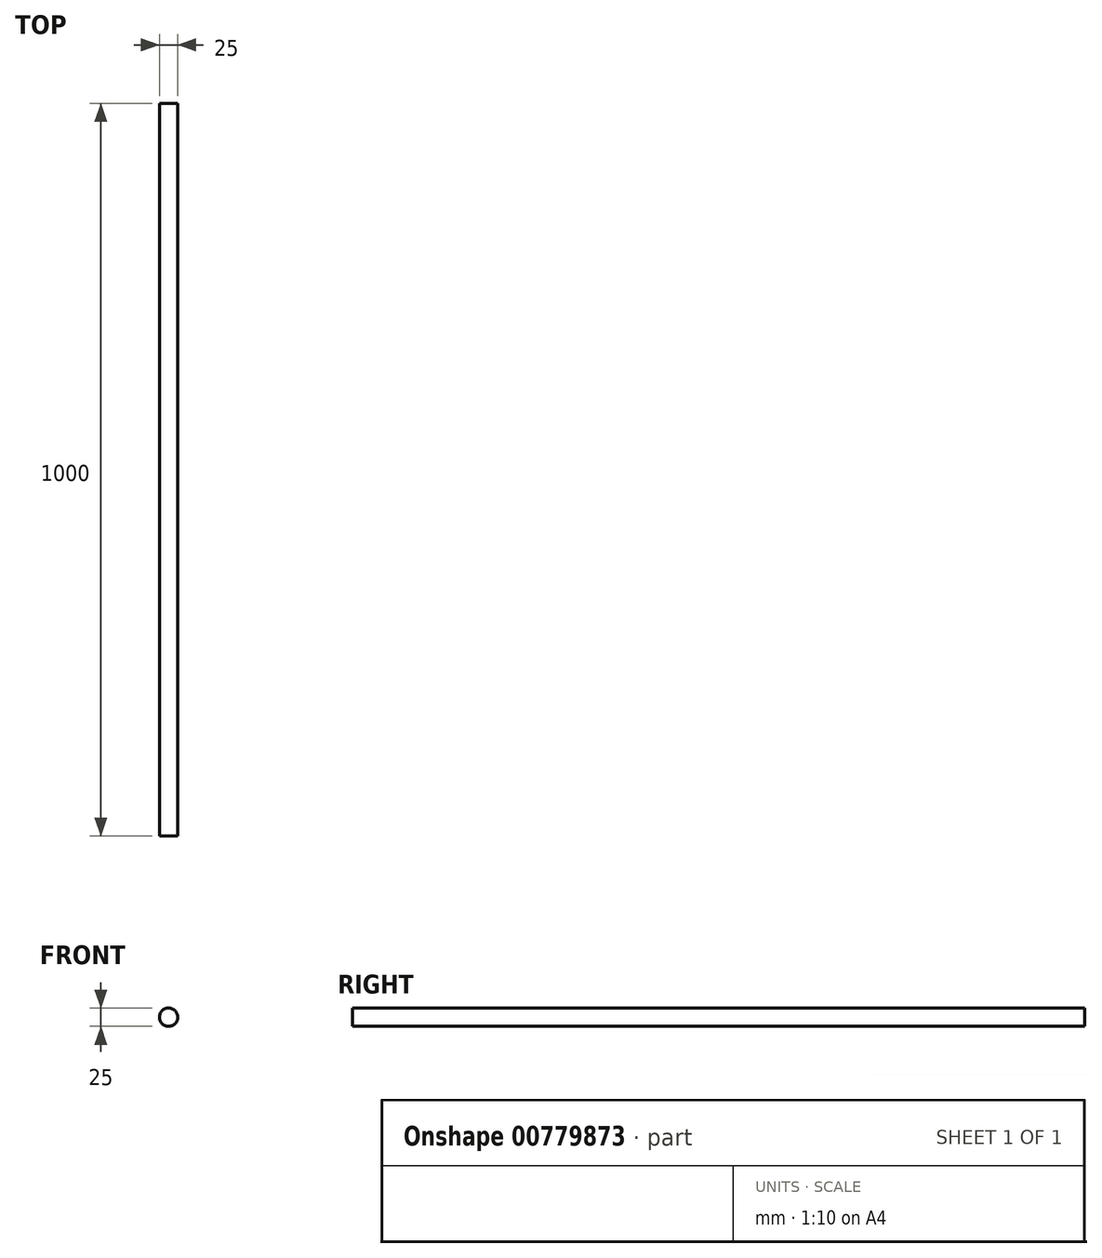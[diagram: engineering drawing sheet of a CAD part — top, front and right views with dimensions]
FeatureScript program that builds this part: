
annotation { "Feature Type Name" : "Feature", "Feature Type Description" : "" }
export const myFeature = defineFeature(function(context is Context, id is Id, definition is map)
    precondition{}
    {
        {
            var Q0;
            Q0=qCreatedBy(makeId("Front.planeOp"),FACE);
            var sketch = newSketch(context, id + "F0", { "sketchPlane" : qUnion([Q0])});
            skCircle(sketch, "E0", {"center": v(0, 0) * mm, "radius": 12.5 * mm});
            skSolve(sketch);
        }
        {
            var Q0;
            Q0=sQuery(id+"F0.wireOp",EDGE,"E0");
            extrude(context, id + "F1", {"bodyType" : ToolBodyType.SURFACE, "surfaceEntities" : qUnion([Q0]), "depth" : 1000 * mm, "offsetDistance" : 25 * mm});
        }
    });
